# Revit family: Toilet-Floor_Mount-KOHLER-Kingston_Comfort_Height-K-25077_1
name_source: partatom
category: Plumbing Fixtures
revit_build: Autodesk Revit 2017 (Build: 20160225_1515(x64)
units: mm (PartAtom-declared; Revit-internal decimal feet)

## family parameters
Cut with Voids When Loaded = No
Host = Face
OmniClass Number = 23.31.19.00
OmniClass Title = Toilets
Part Type = Normal
Room Calculation Point = No
Round Connector Dimension = Use Diameter
Shared = No

## types (6) — shared parameters
ADA Compliant = Yes
Assembly Code = D2010100
CW Connection = Yes
Cold Water Inlet = Cold Water Inlet
Date Modified = 09/04/2020
Default Elevation = 0"
Finish = Kohler-Vitreous_China-0-White
Flow Rate = 0 GPM
Flush Rate- GPF = 1.28 GPF
Flush Rate- LPF = 4.8 LPF
HW Connection = No
Height = 31 1/2"
Hot Water Inlet = Hot Water Inlet
Length = 29 3/4"
Manufacturer = KOHLER Co.
Master Format 2014 = 22 42 13.13
Master Format 2014 Name = Residential Water Closets
Material = Vitreous China
Pressure = 0.00 psi
Product Documentation Link = https://www.us.kohler.com
Product Name = Kingston
Product Page URL = http://www.us.kohler.com
Rough-In = 12"
Seat Included = No
URL = https://www.us.kohler.com
Vent Connection = No
Waste Connection = Yes
Waste Water Outlet = Waste Water Outlet
WaterSense Certified = Yes
Width = 18 3/4"

## per-type parameters (varying)
| type | Description | Left Hand Trip Lever | Model | Right Hand Trip Lever | Type |
| Left Hand Trip Lever, 0-White | Two-piece elongated 1.28 gpf chair height toilet | Yes | K-25077-0 | No | 1 |
| Right Hand Trip Lever, 0-White | Two-piece elongated 1.28 gpf chair height toilet with right-hand trip lever | No | K-25077-RA-0 | Yes | 2 |
| Right Hand Trip Lever, Tank Cover Locks, 0-White | Two-piece elongated 1.28 gpf chair height toilet with right-hand trip lever and tank cover locks | No | K-25077-TR-0 | Yes | 3 |
| Left Hand Trip Lever, Tank Cover Locks, Antimicrobial Finish, 0-White | Two-piece elongated 1.28 gpf chair height toilet with tank cover locks and antimicrobial finish | Yes | K-25077-SST-0 | No | 4 |
| Right Hand Trip Lever, Tank Cover Locks, Antimicrobial Finish, 0-White | Two-piece elongated 1.28 gpf chair height toilet with right-hand trip lever, tank cover locks and antimicrobial finish | No | K-25077-SSTR-0 | Yes | 5 |
| Right Hand Trip Lever, Antimicrobial Finish, 0-White | Two-piece elongated 1.28 gpf chair height toilet with right-hand trip lever and antimicrobial finish | No | K-25077-SSRA-0 | Yes | 6 |

## geometry (parser evidence)
native form markers: Sweep x6
no freeform markers — native parametric forms only
